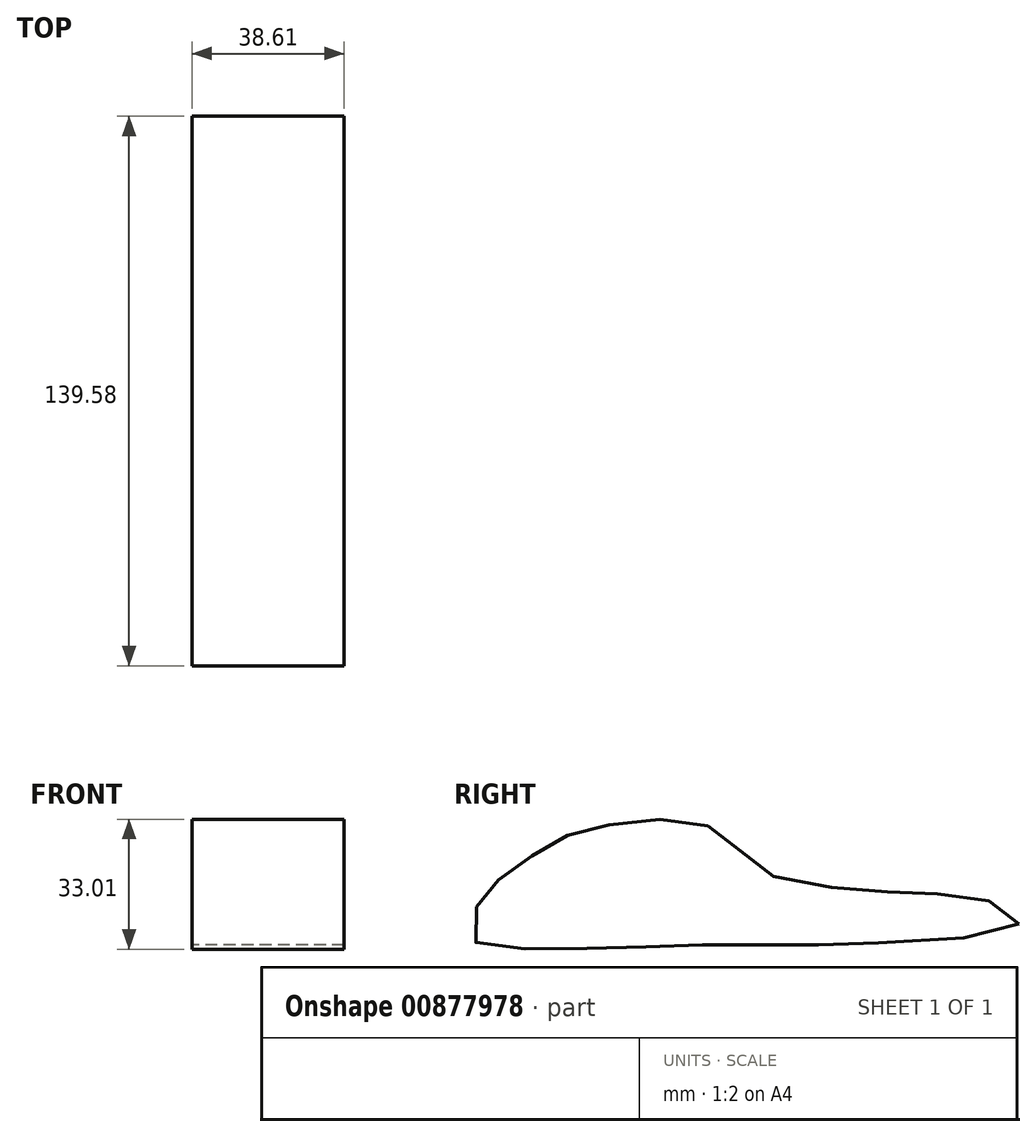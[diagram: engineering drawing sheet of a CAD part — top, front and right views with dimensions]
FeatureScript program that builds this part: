
annotation { "Feature Type Name" : "Feature", "Feature Type Description" : "" }
export const myFeature = defineFeature(function(context is Context, id is Id, definition is map)
    precondition{}
    {
        {
            var Q0;
            Q0=qCreatedBy(makeId("Right.planeOp"),FACE);
            var sketch = newSketch(context, id + "F0", { "sketchPlane" : qUnion([Q0])});
            skFitSpline(sketch, "E0", {"points": [v(72.25, 0) * mm, v(65, 5.7) * mm, v(47.42, 7.76) * mm, v(29.83, 8.8) * mm, v(8.1, 12.93) * mm, v(0, 20.17) * mm, v(-10.17, 26.04) * mm, v(-27.42, 25.7) * mm, v(-40.52, 23.28) * mm, v(-50.18, 18.1) * mm, v(-59.5, 11.55) * mm, v(-64.66, 6.04) * mm, v(-66.73, -3.62) * mm, v(-52.94, -6.38) * mm, v(-28.1, -6.04) * mm, v(-7.07, -5.35) * mm, v(16.04, -5.35) * mm, v(39.83, -4.66) * mm, v(72.25, 0) * mm]});
            skSolve(sketch);
        }
        {
            var Q0;
            Q0 = qSketchRegion(id + "F0", true);
            extrude(context, id + "F1", {"entities" : qUnion([Q0]), "depth" : 38.6 * mm, "offsetDistance" : 25.4 * mm});
        }
    });
